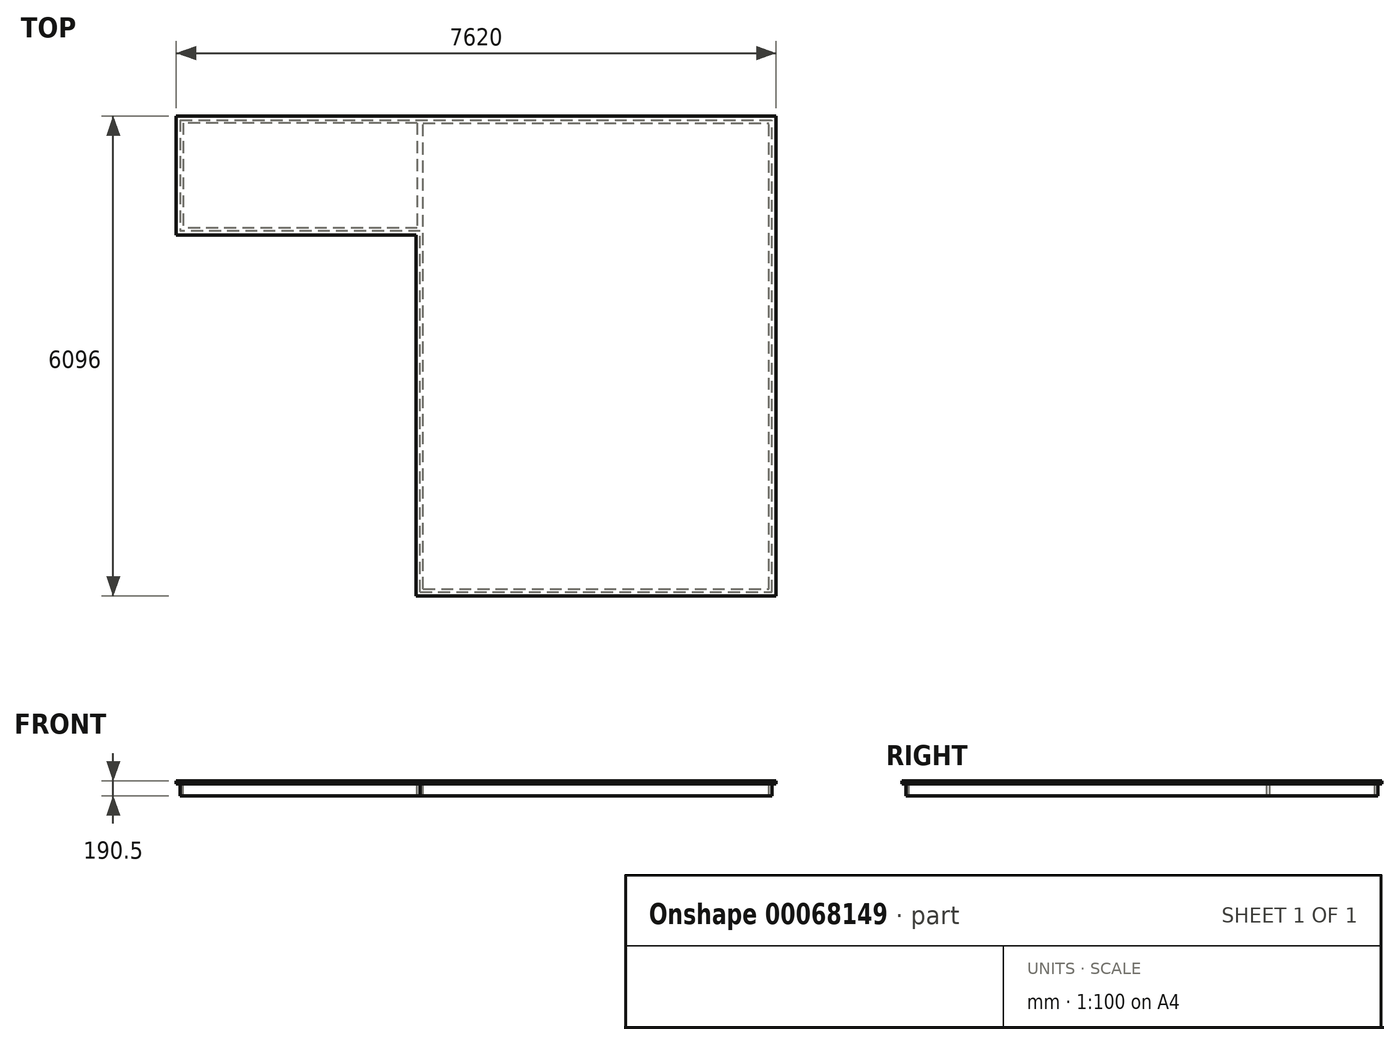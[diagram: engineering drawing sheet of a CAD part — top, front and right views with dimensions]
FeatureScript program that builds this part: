
annotation { "Feature Type Name" : "Feature", "Feature Type Description" : "" }
export const myFeature = defineFeature(function(context is Context, id is Id, definition is map)
    precondition{}
    {
        {
            var Q0;
            Q0=qCreatedBy(makeId("Top.planeOp"),FACE);
            var sketch = newSketch(context, id + "F0", { "sketchPlane" : qUnion([Q0])});
            skLineSegment(sketch, "E0.bottom", {"start": v(623.5, -166.08) * mm, "end": v(5195.5, -166.08) * mm});
            skLineSegment(sketch, "E0.top", {"start": v(623.5, -6262.08) * mm, "end": v(5195.5, -6262.08) * mm});
            skLineSegment(sketch, "E0.left", {"start": v(623.5, -1678.02) * mm, "end": v(623.5, -6262.08) * mm});
            skLineSegment(sketch, "E0.right", {"start": v(5195.5, -166.08) * mm, "end": v(5195.5, -6262.08) * mm});
            skLineSegment(sketch, "E1.bottom", {"start": v(623.5, -166.08) * mm, "end": v(-2424.5, -166.08) * mm});
            skLineSegment(sketch, "E1.top", {"start": v(623.5, -1678.02) * mm, "end": v(-2424.5, -1678.02) * mm});
            skLineSegment(sketch, "E1.right", {"start": v(-2424.5, -166.08) * mm, "end": v(-2424.5, -1678.02) * mm});
            skSolve(sketch);
        }
        {
            var Q0;
            Q0 = qSketchRegion(id + "F0", true);
            extrude(context, id + "F1", {"entities" : qUnion([Q0]), "depth" : 38.1 * mm});
        }
        {
            var Q0;
            Q0=makeQuery(id+"F1.opExtrude","CAP_FACE",FACE,{"disambiguationData":[OSD([sQuery(id+"F0.wireOp",EDGE,"E0.bottom"),sQuery(id+"F0.wireOp",EDGE,"E0.top"),sQuery(id+"F0.wireOp",EDGE,"E0.left"),sQuery(id+"F0.wireOp",EDGE,"E0.right")])],"isStart":true});
            var sketch = newSketch(context, id + "F2", { "sketchPlane" : qUnion([Q0])});
            skLineSegment(sketch, "E2.bottom", {"start": v(674.4, 6211.17) * mm, "end": v(5144.6, 6211.17) * mm});
            skLineSegment(sketch, "E2.top", {"start": v(674.4, 216.88) * mm, "end": v(5144.6, 216.88) * mm});
            skLineSegment(sketch, "E2.left", {"start": v(674.4, 6211.17) * mm, "end": v(674.4, 216.88) * mm});
            skLineSegment(sketch, "E2.right", {"start": v(5144.6, 6211.17) * mm, "end": v(5144.6, 216.88) * mm});
            skLineSegment(sketch, "E3.bottom", {"start": v(712.5, 6173.07) * mm, "end": v(5106.5, 6173.07) * mm});
            skLineSegment(sketch, "E3.top", {"start": v(712.5, 254.98) * mm, "end": v(5106.5, 254.98) * mm});
            skLineSegment(sketch, "E3.left", {"start": v(712.5, 6173.07) * mm, "end": v(712.5, 254.98) * mm});
            skLineSegment(sketch, "E3.right", {"start": v(5106.5, 6173.07) * mm, "end": v(5106.5, 254.98) * mm});
            skSolve(sketch);
        }
        {
            var Q0;
            Q0 = qSketchRegion(id + "F2", true);
            extrude(context, id + "F3", {"entities" : qUnion([Q0]), "operationType" : NewBodyOperationType.ADD, "depth" : 152.4 * mm});
        }
        {
            var Q0;
            {var subQ0=sQuery(id+"F0.wireOp",EDGE,"E0.right");var subQ1=sQuery(id+"F0.wireOp",EDGE,"E0.left");var subQ2=sQuery(id+"F0.wireOp",EDGE,"E0.top");var subQ3=sQuery(id+"F0.wireOp",EDGE,"E1.bottom");var subQ4=sQuery(id+"F0.wireOp",EDGE,"E0.bottom");var subQ5=sQuery(id+"F0.wireOp",EDGE,"E1.top");var subQ6=sQuery(id+"F0.wireOp",EDGE,"E1.right");Q0=makeQuery(id+"F3.boolean.opBoolean","SPLIT",FACE,{"disambiguationData":[TD([makeQuery(id+"F1.opExtrude","SWEPT_FACE",FACE,{"disambiguationData":[OSD([subQ2])]})])],"derivedFrom":makeQuery(id+"F1.opExtrude","CAP_FACE",FACE,{"disambiguationData":[OSD([subQ4,subQ2,subQ1,subQ0,subQ3,subQ5,subQ6])],"isStart":true})});}
            var sketch = newSketch(context, id + "F4", { "sketchPlane" : qUnion([Q0])});
            skLineSegment(sketch, "E4.bottom", {"start": v(674.4, 216.88) * mm, "end": v(-2373.6, 216.88) * mm});
            skLineSegment(sketch, "E4.top", {"start": v(674.4, 1627.22) * mm, "end": v(-2373.6, 1627.22) * mm});
            skLineSegment(sketch, "E4.left", {"start": v(674.4, 216.88) * mm, "end": v(674.4, 1627.22) * mm});
            skLineSegment(sketch, "E4.right", {"start": v(-2373.6, 216.88) * mm, "end": v(-2373.6, 1627.22) * mm});
            skLineSegment(sketch, "E5.0", {"start": v(636.3, 1589.12) * mm, "end": v(-2335.5, 1589.12) * mm});
            skLineSegment(sketch, "E5.1", {"start": v(636.3, 254.98) * mm, "end": v(636.3, 1589.12) * mm});
            skLineSegment(sketch, "E5.2", {"start": v(636.3, 254.98) * mm, "end": v(-2335.5, 254.98) * mm});
            skLineSegment(sketch, "E5.3", {"start": v(-2335.5, 254.98) * mm, "end": v(-2335.5, 1589.12) * mm});
            skSolve(sketch);
        }
        {
            var Q0;
            Q0 = qSketchRegion(id + "F4", true);
            var Q1;
            Q1=makeQuery(id+"F3.opExtrude","CAP_FACE",FACE,{"disambiguationData":[OSD([sQuery(id+"F2.wireOp",EDGE,"E2.bottom"),sQuery(id+"F2.wireOp",EDGE,"E2.top"),sQuery(id+"F2.wireOp",EDGE,"E2.left"),sQuery(id+"F2.wireOp",EDGE,"E2.right"),sQuery(id+"F2.wireOp",EDGE,"E3.bottom"),sQuery(id+"F2.wireOp",EDGE,"E3.top"),sQuery(id+"F2.wireOp",EDGE,"E3.left"),sQuery(id+"F2.wireOp",EDGE,"E3.right")])],"isStart":false});
            extrude(context, id + "F5", {"entities" : qUnion([Q0]), "operationType" : NewBodyOperationType.ADD, "endBound" : BoundingType.UP_TO_SURFACE, "endBoundEntityFace" : qUnion([Q1]), "depth" : 30.48 * mm});
        }
    });
